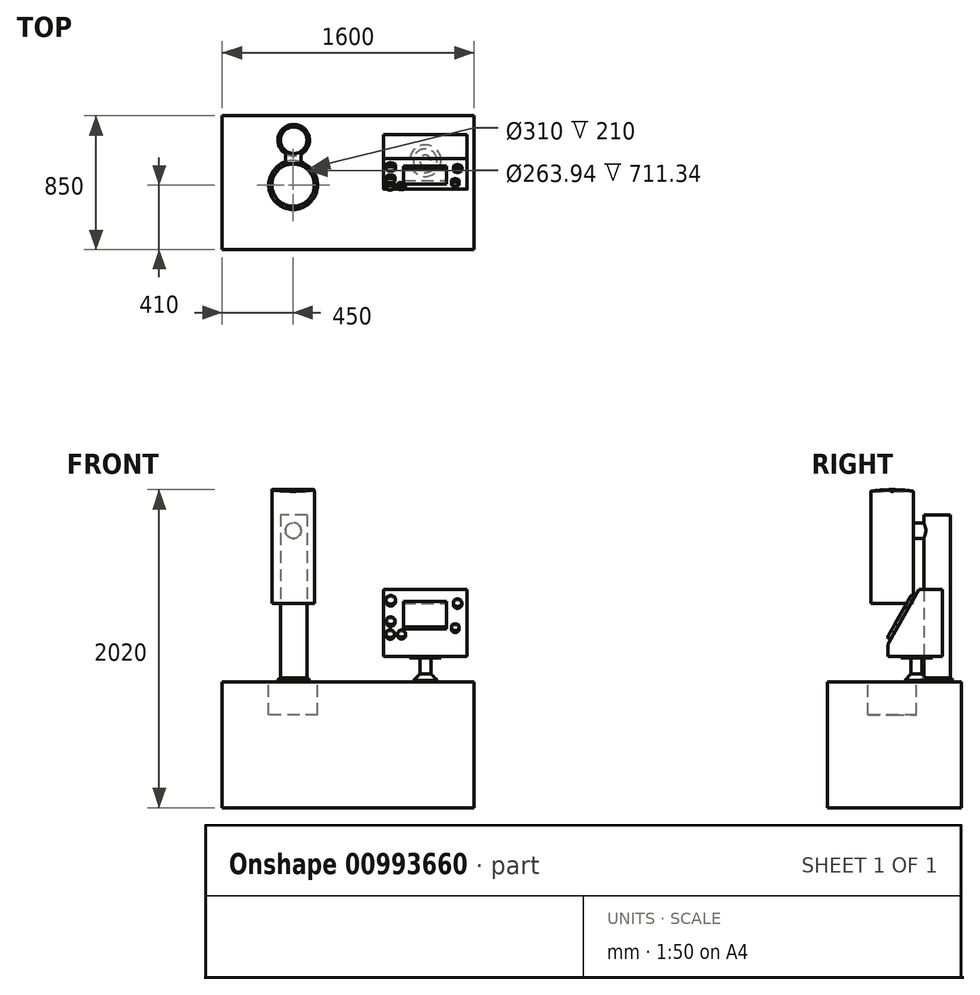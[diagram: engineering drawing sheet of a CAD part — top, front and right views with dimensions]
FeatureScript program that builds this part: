
annotation { "Feature Type Name" : "Feature", "Feature Type Description" : "" }
export const myFeature = defineFeature(function(context is Context, id is Id, definition is map)
    precondition{}
    {
        {
            var Q0;
            Q0=qCreatedBy(makeId("Top.planeOp"),FACE);
            var sketch = newSketch(context, id + "F0", { "sketchPlane" : qUnion([Q0])});
            skLineSegment(sketch, "E0.bottom", {"start": v(800, -425) * mm, "end": v(-800, -425) * mm});
            skLineSegment(sketch, "E0.top", {"start": v(800, 425) * mm, "end": v(-800, 425) * mm});
            skLineSegment(sketch, "E0.left", {"start": v(800, -425) * mm, "end": v(800, 425) * mm});
            skLineSegment(sketch, "E0.right", {"start": v(-800, -425) * mm, "end": v(-800, 425) * mm});
            skPoint(sketch, "E0.middle", {"position": v(0, 0) * mm});
            skSolve(sketch);
        }
        {
            var Q0;
            Q0 = qSketchRegion(id + "F0", true);
            extrude(context, id + "F1", {"entities" : qUnion([Q0]), "oppositeDirection" : true, "depth" : 800 * mm, "offsetDistance" : 25.4 * mm});
        }
        {
            var Q0;
            Q0=makeQuery(id+"F1.opExtrude","CAP_FACE",FACE,{"disambiguationData":[OSD([sQuery(id+"F0.wireOp",EDGE,"E0.bottom"),sQuery(id+"F0.wireOp",EDGE,"E0.top"),sQuery(id+"F0.wireOp",EDGE,"E0.left"),sQuery(id+"F0.wireOp",EDGE,"E0.right")])],"isStart":true});
            var sketch = newSketch(context, id + "F2", { "sketchPlane" : qUnion([Q0])});
            skCircle(sketch, "E1", {"center": v(-350, -15) * mm, "radius": 155 * mm});
            skSolve(sketch);
        }
        {
            var Q0;
            Q0=makeQuery(id+"F2.imprint","IMPRINT",FACE,{"disambiguationData":[TD([[makeQuery(id+"F2.imprint","IMPRINT",EDGE,{"derivedFrom":sQuery(id+"F2.wireOp",EDGE,"E1")}),1.0]])]});
            extrude(context, id + "F3", {"entities" : qUnion([Q0]), "operationType" : NewBodyOperationType.REMOVE, "oppositeDirection" : true, "depth" : 210 * mm, "offsetDistance" : 25.4 * mm});
        }
        {
            var Q0;
            Q0=makeQuery(id+"F1.opExtrude","CAP_FACE",FACE,{"disambiguationData":[OSD([sQuery(id+"F0.wireOp",EDGE,"E0.bottom"),sQuery(id+"F0.wireOp",EDGE,"E0.top"),sQuery(id+"F0.wireOp",EDGE,"E0.left"),sQuery(id+"F0.wireOp",EDGE,"E0.right")])],"isStart":true});
            var sketch = newSketch(context, id + "F4", { "sketchPlane" : qUnion([Q0])});
            skCircle(sketch, "E2", {"center": v(-345.83, 269.97) * mm, "radius": 100 * mm});
            skSolve(sketch);
        }
        {
            var Q0;
            Q0 = qSketchRegion(id + "F4", true);
            extrude(context, id + "F5", {"entities" : qUnion([Q0]), "operationType" : NewBodyOperationType.ADD, "depth" : 25.4 * mm, "offsetDistance" : 25.4 * mm, "hasDraft" : true, "draftAngle" : 6 * degree, "draftPullDirection" : true});
        }
        {
            var Q0;
            Q0=makeQuery(id+"F5.opExtrude","CAP_EDGE",EDGE,{"disambiguationData":[OSD([sQuery(id+"F4.wireOp",EDGE,"E2")])],"isStart":false});
            chamfer(context, id + "F6", {"entities" : qUnion([Q0]), "width" : 12.7 * mm, "tangentPropagation" : true});
        }
        {
            var Q0;
            Q0=makeQuery(id+"F5.opExtrude","CAP_FACE",FACE,{"disambiguationData":[OSD([sQuery(id+"F4.wireOp",EDGE,"E2")])],"isStart":false});
            var sketch = newSketch(context, id + "F7", { "sketchPlane" : qUnion([Q0])});
            skCircle(sketch, "E3", {"center": v(-345.83, 269.97) * mm, "radius": 84.63 * mm});
            skSolve(sketch);
        }
        {
            var Q0;
            Q0 = qSketchRegion(id + "F7", true);
            extrude(context, id + "F8", {"entities" : qUnion([Q0]), "operationType" : NewBodyOperationType.ADD, "depth" : 1060 * mm - 25.4 * mm, "offsetDistance" : 25.4 * mm});
        }
        {
            var Q0;
            Q0=makeQuery(id+"F1.opExtrude","CAP_FACE",FACE,{"disambiguationData":[OSD([sQuery(id+"F0.wireOp",EDGE,"E0.bottom"),sQuery(id+"F0.wireOp",EDGE,"E0.top"),sQuery(id+"F0.wireOp",EDGE,"E0.left"),sQuery(id+"F0.wireOp",EDGE,"E0.right")])],"isStart":true});
            var sketch = newSketch(context, id + "F9", { "sketchPlane" : qUnion([Q0])});
            skCircle(sketch, "E4", {"center": v(490, 140) * mm, "radius": 75 * mm});
            skSolve(sketch);
        }
        {
            var Q0;
            Q0 = qSketchRegion(id + "F9", true);
            extrude(context, id + "F10", {"entities" : qUnion([Q0]), "operationType" : NewBodyOperationType.ADD, "depth" : 50 * mm, "offsetDistance" : 25.4 * mm});
        }
        {
            var Q0;
            Q0=makeQuery(id+"F10.opExtrude","CAP_EDGE",EDGE,{"disambiguationData":[OSD([sQuery(id+"F9.wireOp",EDGE,"E4")])],"isStart":false});
            chamfer(context, id + "F11", {"entities" : qUnion([Q0]), "width" : 40 * mm, "tangentPropagation" : true});
        }
        {
            var Q0;
            Q0=makeQuery(id+"F10.opExtrude","CAP_FACE",FACE,{"disambiguationData":[OSD([sQuery(id+"F9.wireOp",EDGE,"E4")])],"isStart":false});
            var sketch = newSketch(context, id + "F12", { "sketchPlane" : qUnion([Q0])});
            skCircle(sketch, "E5", {"center": v(490, 140) * mm, "radius": 35 * mm});
            skSolve(sketch);
        }
        {
            var Q0;
            Q0 = qSketchRegion(id + "F12", true);
            extrude(context, id + "F13", {"entities" : qUnion([Q0]), "operationType" : NewBodyOperationType.ADD, "depth" : 100 * mm, "offsetDistance" : 25.4 * mm});
        }
        {
            var Q0;
            Q0=makeQuery(id+"F13.opExtrude","CAP_FACE",FACE,{"disambiguationData":[OSD([sQuery(id+"F12.wireOp",EDGE,"E5")])],"isStart":false});
            var sketch = newSketch(context, id + "F14", { "sketchPlane" : qUnion([Q0])});
            skCircle(sketch, "E6", {"center": v(490, 140) * mm, "radius": 100 * mm});
            skSolve(sketch);
        }
        {
            var Q0;
            Q0 = qSketchRegion(id + "F14", true);
            extrude(context, id + "F15", {"entities" : qUnion([Q0]), "operationType" : NewBodyOperationType.ADD, "depth" : 10 * mm, "offsetDistance" : 25.4 * mm});
        }
        {
            var Q0;
            Q0=makeQuery(id+"F15.opExtrude","CAP_EDGE",EDGE,{"disambiguationData":[OSD([sQuery(id+"F14.wireOp",EDGE,"E6")])],"isStart":false});
            cPlane(context, id + "F16", {"entities" : qUnion([Q0]), "cplaneType" : CPlaneType.LINE_ANGLE, "offset" : 25.4 * mm, "angle" : 0 * degree, "width" : 152.4 * mm, "height" : 152.4 * mm});
        }
        {
            var Q0;
            Q0=qCreatedBy(id+"F16.planeOp",FACE);
            var sketch = newSketch(context, id + "F17", { "sketchPlane" : qUnion([Q0])});
            skLineSegment(sketch, "E7", {"start": v(154.35, 585) * mm, "end": v(304.35, 585) * mm});
            skLineSegment(sketch, "E8", {"start": v(304.35, 585) * mm, "end": v(304.35, 160) * mm});
            skLineSegment(sketch, "E9", {"start": v(304.35, 160) * mm, "end": v(-40.65, 160) * mm});
            skLineSegment(sketch, "E10", {"start": v(-40.65, 160) * mm, "end": v(-40.65, 229.48) * mm});
            skLineSegment(sketch, "E11", {"start": v(-35.47, 249.16) * mm, "end": v(154.35, 585) * mm});
            skPoint(sketch, "E12.visualSharp", {"position": v(-40.65, 240) * mm});
            skArc(sketch, "E12.filletArc", {"start": v(-35.47, 249.16) * mm, "mid": v(-39.33, 239.65) * mm, "end": v(-40.65, 229.48) * mm});
            skSolve(sketch);
        }
        {
            var Q0;
            Q0 = qSketchRegion(id + "F17", true);
            extrude(context, id + "F18", {"entities" : qUnion([Q0]), "operationType" : NewBodyOperationType.ADD, "endBound" : BoundingType.SYMMETRIC, "depth" : 530 * mm, "offsetDistance" : 25.4 * mm});
        }
        {
            var Q0;
            Q0=makeQuery(id+"F8.opExtrude","CAP_EDGE",EDGE,{"disambiguationData":[OSD([sQuery(id+"F7.wireOp",EDGE,"E3")])],"isStart":false});
            cPlane(context, id + "F19", {"entities" : qUnion([Q0]), "cplaneType" : CPlaneType.LINE_ANGLE, "offset" : 25.4 * mm, "angle" : 90 * degree, "width" : 152.4 * mm, "height" : 152.4 * mm});
        }
        {
            var Q0;
            Q0=qCreatedBy(id+"F19.planeOp",FACE);
            var sketch = newSketch(context, id + "F20", { "sketchPlane" : qUnion([Q0])});
            skCircle(sketch, "E13", {"center": v(349.12, 960) * mm, "radius": 50 * mm});
            skSolve(sketch);
        }
        {
            var Q0;
            Q0 = qSketchRegion(id + "F20", true);
            extrude(context, id + "F21", {"entities" : qUnion([Q0]), "operationType" : NewBodyOperationType.ADD, "oppositeDirection" : true, "depth" : 150 * mm, "offsetDistance" : 25.4 * mm});
        }
        {
            var Q0;
            Q0=makeQuery(id+"F8.opExtrude","CAP_FACE",FACE,{"disambiguationData":[OSD([sQuery(id+"F7.wireOp",EDGE,"E3")])],"isStart":false});
            var sketch = newSketch(context, id + "F22", { "sketchPlane" : qUnion([Q0])});
            skCircle(sketch, "E14", {"center": v(-350, -15) * mm, "radius": 134.97 * mm});
            skCircle(sketch, "E15", {"center": v(-350, -15) * mm, "radius": 131.97 * mm});
            skSolve(sketch);
        }
        {
            var Q0;
            Q0 = qSketchRegion(id + "F22", true);
            extrude(context, id + "F23", {"entities" : qUnion([Q0]), "oppositeDirection" : true, "depth" : 561.34 * mm, "offsetDistance" : 25.4 * mm});
        }
        {
            var Q0;
            Q0=makeQuery(id+"F23.opExtrude","CAP_FACE",FACE,{"disambiguationData":[OSD([sQuery(id+"F22.wireOp",EDGE,"E14"),sQuery(id+"F22.wireOp",EDGE,"E15")])],"isStart":true});
            var sketch = newSketch(context, id + "F24", { "sketchPlane" : qUnion([Q0])});
            skCircle(sketch, "E16", {"center": v(-350, -15) * mm, "radius": 131.97 * mm});
            skCircle(sketch, "E17", {"center": v(-350, -15) * mm, "radius": 134.97 * mm});
            skSolve(sketch);
        }
        {
            var Q0;
            Q0 = qSketchRegion(id + "F24", true);
            extrude(context, id + "F25", {"entities" : qUnion([Q0]), "operationType" : NewBodyOperationType.ADD, "depth" : 150 * mm, "offsetDistance" : 25.4 * mm});
        }
        {
            var Q0;
            Q0=makeQuery(id+"F25.opExtrude","CAP_EDGE",EDGE,{"disambiguationData":[OSD([sQuery(id+"F24.wireOp",EDGE,"E17")])],"isStart":false});
            cPlane(context, id + "F26", {"entities" : qUnion([Q0]), "cplaneType" : CPlaneType.LINE_ANGLE, "offset" : 25.4 * mm, "angle" : 0 * degree, "width" : 152.4 * mm, "height" : 152.4 * mm});
        }
        {
            var Q0;
            Q0=qCreatedBy(id+"F26.planeOp",FACE);
            var sketch = newSketch(context, id + "F27", { "sketchPlane" : qUnion([Q0])});
            skArc(sketch, "E18", {"start": v(119.31, 1210) * mm, "mid": v(-15.22, 1220) * mm, "end": v(-149.75, 1210) * mm});
            skLineSegment(sketch, "E19", {"start": v(119.31, 1210) * mm, "end": v(-149.75, 1210) * mm});
            skSolve(sketch);
        }
        {
            var Q0;
            Q0 = qSketchRegion(id + "F27", true);
            extrude(context, id + "F28", {"entities" : qUnion([Q0]), "operationType" : NewBodyOperationType.ADD, "endBound" : BoundingType.SYMMETRIC, "oppositeDirection" : true, "depth" : 269.5 * mm, "offsetDistance" : 25.4 * mm});
        }
        {
            var Q0;
            {var subQ0=sQuery(id+"F27.wireOp",EDGE,"E18");var subQ1=sQuery(id+"F24.wireOp",EDGE,"E17");var subQ2=sQuery(id+"F27.wireOp",EDGE,"E19");Q0=makeQuery(id+"F28.boolean.opBoolean","SPLIT",FACE,{"disambiguationData":[TD([makeQuery(id+"F23.opExtrude","SWEPT_FACE",FACE,{"disambiguationData":[OSD([sQuery(id+"F22.wireOp",EDGE,"E14")])]}),makeQuery(id+"F25.opExtrude","CAP_FACE",FACE,{"disambiguationData":[OSD([sQuery(id+"F24.wireOp",EDGE,"E16"),subQ1])],"isStart":false}),makeQuery(id+"F25.opExtrude","SWEPT_FACE",FACE,{"disambiguationData":[OSD([subQ1])]}),makeQuery(id+"F28.opExtrude","SWEPT_FACE",FACE,{"disambiguationData":[OSD([subQ0])]}),makeQuery(id+"F28.opExtrude","CAP_FACE",FACE,{"disambiguationData":[OSD([subQ0,subQ2])],"isStart":false})]),OD(0.0)],"derivedFrom":makeQuery(id+"F28.opExtrude","SWEPT_FACE",FACE,{"disambiguationData":[OSD([subQ2])]})});}
            var sketch = newSketch(context, id + "F29", { "sketchPlane" : qUnion([Q0])});
            skLineSegment(sketch, "E20", {"start": v(-484.75, -119.31) * mm, "end": v(-363.3, -119.31) * mm});
            skArc(sketch, "E21", {"start": v(-484.75, 7.25) * mm, "mid": v(-447.38, -78.45) * mm, "end": v(-363.3, -119.31) * mm});
            skLineSegment(sketch, "E22", {"start": v(-484.75, -119.31) * mm, "end": v(-484.75, 7.25) * mm});
            skSolve(sketch);
        }
        {
            var Q0;
            Q0 = qSketchRegion(id + "F29", true);
            extrude(context, id + "F30", {"entities" : qUnion([Q0]), "operationType" : NewBodyOperationType.REMOVE, "oppositeDirection" : true, "depth" : 25.4 * mm, "offsetDistance" : 25.4 * mm});
        }
        {
            var Q0;
            {var subQ0=sQuery(id+"F27.wireOp",EDGE,"E18");var subQ1=sQuery(id+"F24.wireOp",EDGE,"E17");var subQ2=sQuery(id+"F27.wireOp",EDGE,"E19");Q0=makeQuery(id+"F28.boolean.opBoolean","SPLIT",FACE,{"disambiguationData":[TD([makeQuery(id+"F23.opExtrude","SWEPT_FACE",FACE,{"disambiguationData":[OSD([sQuery(id+"F22.wireOp",EDGE,"E14")])]}),makeQuery(id+"F25.opExtrude","CAP_FACE",FACE,{"disambiguationData":[OSD([sQuery(id+"F24.wireOp",EDGE,"E16"),subQ1])],"isStart":false}),makeQuery(id+"F25.opExtrude","SWEPT_FACE",FACE,{"disambiguationData":[OSD([subQ1])]}),makeQuery(id+"F28.opExtrude","SWEPT_FACE",FACE,{"disambiguationData":[OSD([subQ0])]}),makeQuery(id+"F28.opExtrude","CAP_FACE",FACE,{"disambiguationData":[OSD([subQ0,subQ2])],"isStart":false})]),OD(1.0)],"derivedFrom":makeQuery(id+"F28.opExtrude","SWEPT_FACE",FACE,{"disambiguationData":[OSD([subQ2])]})});}
            var sketch = newSketch(context, id + "F31", { "sketchPlane" : qUnion([Q0])});
            skLineSegment(sketch, "E23", {"start": v(-484.75, 149.75) * mm, "end": v(-357.75, 149.75) * mm});
            skArc(sketch, "E24", {"start": v(-357.75, 149.75) * mm, "mid": v(-445.44, 110.44) * mm, "end": v(-484.75, 22.75) * mm});
            skLineSegment(sketch, "E25", {"start": v(-484.75, 22.75) * mm, "end": v(-484.75, 149.75) * mm});
            skSolve(sketch);
        }
        {
            var Q0;
            Q0 = qSketchRegion(id + "F31", true);
            extrude(context, id + "F32", {"entities" : qUnion([Q0]), "operationType" : NewBodyOperationType.REMOVE, "oppositeDirection" : true, "depth" : 25.4 * mm, "offsetDistance" : 25.4 * mm});
        }
        {
            var Q0;
            {var subQ0=sQuery(id+"F27.wireOp",EDGE,"E18");var subQ1=sQuery(id+"F24.wireOp",EDGE,"E17");var subQ2=sQuery(id+"F27.wireOp",EDGE,"E19");Q0=makeQuery(id+"F28.boolean.opBoolean","SPLIT",FACE,{"disambiguationData":[TD([makeQuery(id+"F23.opExtrude","SWEPT_FACE",FACE,{"disambiguationData":[OSD([sQuery(id+"F22.wireOp",EDGE,"E14")])]}),makeQuery(id+"F25.opExtrude","CAP_FACE",FACE,{"disambiguationData":[OSD([sQuery(id+"F24.wireOp",EDGE,"E16"),subQ1])],"isStart":false}),makeQuery(id+"F25.opExtrude","SWEPT_FACE",FACE,{"disambiguationData":[OSD([subQ1])]}),makeQuery(id+"F28.opExtrude","SWEPT_FACE",FACE,{"disambiguationData":[OSD([subQ0])]}),makeQuery(id+"F28.opExtrude","CAP_FACE",FACE,{"disambiguationData":[OSD([subQ0,subQ2])],"isStart":true})]),OD(0.0)],"derivedFrom":makeQuery(id+"F28.opExtrude","SWEPT_FACE",FACE,{"disambiguationData":[OSD([subQ2])]})});}
            var sketch = newSketch(context, id + "F33", { "sketchPlane" : qUnion([Q0])});
            skLineSegment(sketch, "E26", {"start": v(-215.25, -119.31) * mm, "end": v(-336.7, -119.31) * mm});
            skArc(sketch, "E27", {"start": v(-336.7, -119.31) * mm, "mid": v(-252.62, -78.45) * mm, "end": v(-215.25, 7.25) * mm});
            skLineSegment(sketch, "E28", {"start": v(-215.25, 7.25) * mm, "end": v(-215.25, -119.31) * mm});
            skSolve(sketch);
        }
        {
            var Q0;
            Q0 = qSketchRegion(id + "F33", true);
            extrude(context, id + "F34", {"entities" : qUnion([Q0]), "operationType" : NewBodyOperationType.REMOVE, "oppositeDirection" : true, "depth" : 25.4 * mm, "offsetDistance" : 25.4 * mm});
        }
        {
            var Q0;
            {var subQ0=sQuery(id+"F27.wireOp",EDGE,"E18");var subQ1=sQuery(id+"F24.wireOp",EDGE,"E17");var subQ2=sQuery(id+"F27.wireOp",EDGE,"E19");Q0=makeQuery(id+"F28.boolean.opBoolean","SPLIT",FACE,{"disambiguationData":[TD([makeQuery(id+"F23.opExtrude","SWEPT_FACE",FACE,{"disambiguationData":[OSD([sQuery(id+"F22.wireOp",EDGE,"E14")])]}),makeQuery(id+"F25.opExtrude","CAP_FACE",FACE,{"disambiguationData":[OSD([sQuery(id+"F24.wireOp",EDGE,"E16"),subQ1])],"isStart":false}),makeQuery(id+"F25.opExtrude","SWEPT_FACE",FACE,{"disambiguationData":[OSD([subQ1])]}),makeQuery(id+"F28.opExtrude","SWEPT_FACE",FACE,{"disambiguationData":[OSD([subQ0])]}),makeQuery(id+"F28.opExtrude","CAP_FACE",FACE,{"disambiguationData":[OSD([subQ0,subQ2])],"isStart":true})]),OD(1.0)],"derivedFrom":makeQuery(id+"F28.opExtrude","SWEPT_FACE",FACE,{"disambiguationData":[OSD([subQ2])]})});}
            var sketch = newSketch(context, id + "F35", { "sketchPlane" : qUnion([Q0])});
            skLineSegment(sketch, "E29", {"start": v(-215.25, 149.75) * mm, "end": v(-215.25, 22.75) * mm});
            skArc(sketch, "E30", {"start": v(-215.25, 22.75) * mm, "mid": v(-254.56, 110.44) * mm, "end": v(-342.25, 149.75) * mm});
            skLineSegment(sketch, "E31", {"start": v(-342.25, 149.75) * mm, "end": v(-215.25, 149.75) * mm});
            skSolve(sketch);
        }
        {
            var Q0;
            Q0 = qSketchRegion(id + "F35", true);
            extrude(context, id + "F36", {"entities" : qUnion([Q0]), "operationType" : NewBodyOperationType.REMOVE, "oppositeDirection" : true, "depth" : 25.4 * mm, "offsetDistance" : 25.4 * mm});
        }
        {
            var Q0;
            Q0=makeQuery(id+"F18.opExtrude","SWEPT_FACE",FACE,{"disambiguationData":[OSD([sQuery(id+"F17.wireOp",EDGE,"E11")])]});
            var sketch = newSketch(context, id + "F37", { "sketchPlane" : qUnion([Q0])});
            skCircle(sketch, "E32", {"center": v(269.71, 497.25) * mm, "radius": 31.03 * mm});
            skCircle(sketch, "E33", {"center": v(269.71, 344.76) * mm, "radius": 27.9 * mm});
            skCircle(sketch, "E34", {"center": v(266.87, 250.47) * mm, "radius": 27.52 * mm});
            skCircle(sketch, "E35", {"center": v(338.7, 250.47) * mm, "radius": 25.37 * mm});
            skCircle(sketch, "E36", {"center": v(694.38, 476.2) * mm, "radius": 27.02 * mm});
            skCircle(sketch, "E37", {"center": v(679.87, 297.54) * mm, "radius": 24.8 * mm});
            skLineSegment(sketch, "E38.bottom", {"start": v(351.84, 485.93) * mm, "end": v(624.48, 485.93) * mm});
            skLineSegment(sketch, "E38.top", {"start": v(351.84, 298.12) * mm, "end": v(624.48, 298.12) * mm});
            skLineSegment(sketch, "E38.left", {"start": v(351.84, 485.93) * mm, "end": v(351.84, 298.12) * mm});
            skLineSegment(sketch, "E38.right", {"start": v(624.48, 485.93) * mm, "end": v(624.48, 298.12) * mm});
            skSolve(sketch);
        }
        {
            var Q0;
            Q0 = qSketchRegion(id + "F37", true);
            extrude(context, id + "F38", {"entities" : qUnion([Q0]), "operationType" : NewBodyOperationType.ADD, "depth" : 25.4 * mm, "offsetDistance" : 25.4 * mm});
        }
    });
